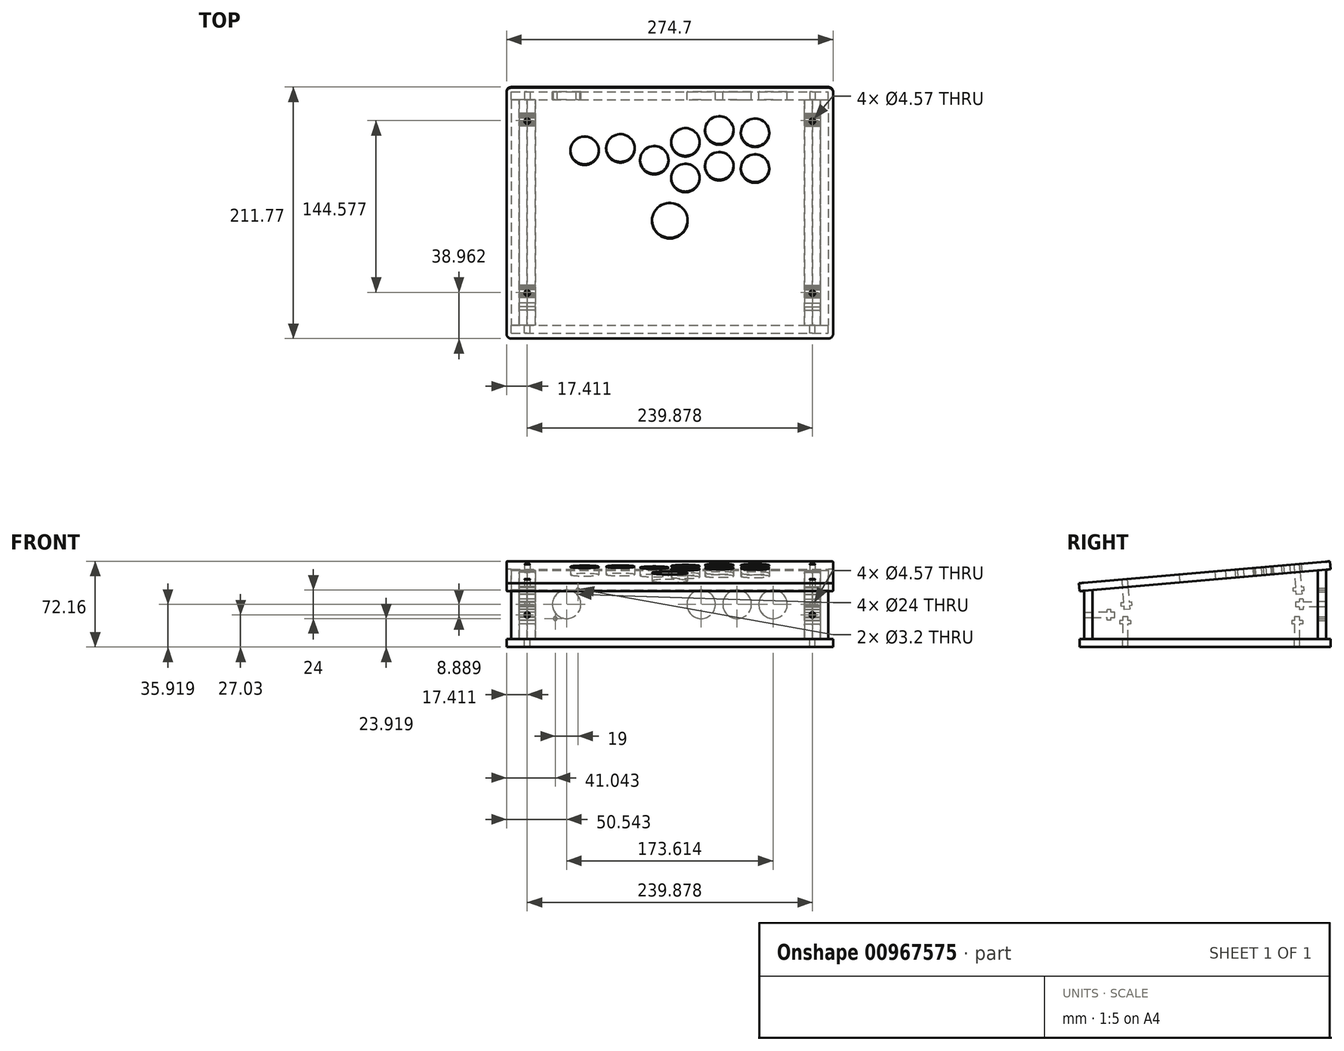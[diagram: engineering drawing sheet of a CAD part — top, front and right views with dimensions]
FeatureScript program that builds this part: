
annotation { "Feature Type Name" : "Feature", "Feature Type Description" : "" }
export const myFeature = defineFeature(function(context is Context, id is Id, definition is map)
    precondition{}
    {
        {
            var Q0;
            Q0=qCreatedBy(makeId("Right.planeOp"),FACE);
            var sketch = newSketch(context, id + "F0", { "sketchPlane" : qUnion([Q0])});
            skLineSegment(sketch, "E0", {"start": v(-101.6, -20.32) * mm, "end": v(101.6, -20.32) * mm});
            skLineSegment(sketch, "E1", {"start": v(101.6, -20.32) * mm, "end": v(101.6, 38.1) * mm});
            skLineSegment(sketch, "E2", {"start": v(101.6, 38.1) * mm, "end": v(-101.6, 20.32) * mm});
            skLineSegment(sketch, "E3", {"start": v(-101.6, 20.32) * mm, "end": v(-101.6, -20.32) * mm});
            skLineSegment(sketch, "E4", {"start": v(94.9, 37.51) * mm, "end": v(94.9, -20.32) * mm});
            skLineSegment(sketch, "E5", {"start": v(-94.9, 20.9) * mm, "end": v(-94.9, -20.32) * mm});
            skLineSegment(sketch, "E6", {"start": v(79.65, -20.32) * mm, "end": v(79.65, -1.63) * mm});
            skLineSegment(sketch, "E7", {"start": v(79.65, -1.63) * mm, "end": v(75.08, -1.63) * mm});
            skLineSegment(sketch, "E8", {"start": v(75.08, -1.63) * mm, "end": v(75.08, -20.32) * mm});
            skLineSegment(sketch, "E9", {"start": v(-64.92, -20.32) * mm, "end": v(-64.92, -1.63) * mm});
            skLineSegment(sketch, "E10", {"start": v(-64.92, -1.63) * mm, "end": v(-69.5, -1.63) * mm});
            skLineSegment(sketch, "E11", {"start": v(-69.5, -1.63) * mm, "end": v(-69.5, -20.32) * mm});
            skLineSegment(sketch, "E12", {"start": v(79.71, 36.18) * mm, "end": v(81.34, 17.56) * mm});
            skLineSegment(sketch, "E13", {"start": v(81.34, 17.56) * mm, "end": v(76.79, 17.16) * mm});
            skLineSegment(sketch, "E14", {"start": v(76.79, 17.16) * mm, "end": v(75.16, 35.78) * mm});
            skLineSegment(sketch, "E15", {"start": v(-65.04, 23.52) * mm, "end": v(-63.4, 4.9) * mm});
            skLineSegment(sketch, "E16", {"start": v(-63.4, 4.9) * mm, "end": v(-67.96, 4.5) * mm});
            skLineSegment(sketch, "E17", {"start": v(-67.96, 4.5) * mm, "end": v(-69.6, 23.12) * mm});
            skLineSegment(sketch, "E18", {"start": v(94.9, 6.6) * mm, "end": v(76.2, 6.6) * mm});
            skLineSegment(sketch, "E19", {"start": v(76.2, 6.6) * mm, "end": v(76.2, 11.17) * mm});
            skLineSegment(sketch, "E20", {"start": v(76.2, 11.17) * mm, "end": v(94.9, 11.17) * mm});
            skLineSegment(sketch, "E21", {"start": v(-94.9, -2.29) * mm, "end": v(-76.2, -2.29) * mm});
            skLineSegment(sketch, "E22", {"start": v(-76.2, -2.29) * mm, "end": v(-76.2, 2.29) * mm});
            skLineSegment(sketch, "E23", {"start": v(-76.2, 2.29) * mm, "end": v(-94.9, 2.29) * mm});
            skPoint(sketch, "E24", {"position": v(-76.2, 0) * mm});
            skPoint(sketch, "E25", {"position": v(76.2, 8.89) * mm});
            skPoint(sketch, "E26", {"position": v(101.6, 8.89) * mm});
            skPoint(sketch, "E27", {"position": v(-101.6, 0) * mm});
            skLineSegment(sketch, "E28.bottom", {"start": v(81.94, -4.67) * mm, "end": v(72.8, -4.67) * mm});
            skLineSegment(sketch, "E28.top", {"start": v(81.94, -7.72) * mm, "end": v(72.8, -7.72) * mm});
            skLineSegment(sketch, "E28.left", {"start": v(81.94, -4.67) * mm, "end": v(81.94, -7.72) * mm});
            skLineSegment(sketch, "E28.right", {"start": v(72.8, -4.67) * mm, "end": v(72.8, -7.72) * mm});
            skLineSegment(sketch, "E29.bottom", {"start": v(-62.64, -4.67) * mm, "end": v(-71.78, -4.67) * mm});
            skLineSegment(sketch, "E29.top", {"start": v(-62.64, -7.72) * mm, "end": v(-71.78, -7.72) * mm});
            skLineSegment(sketch, "E29.left", {"start": v(-62.64, -4.67) * mm, "end": v(-62.64, -7.72) * mm});
            skLineSegment(sketch, "E29.right", {"start": v(-71.78, -4.67) * mm, "end": v(-71.78, -7.72) * mm});
            skLineSegment(sketch, "E30.bottom", {"start": v(-79.25, -4.57) * mm, "end": v(-82.3, -4.57) * mm});
            skLineSegment(sketch, "E30.top", {"start": v(-79.25, 4.57) * mm, "end": v(-82.3, 4.57) * mm});
            skLineSegment(sketch, "E30.left", {"start": v(-79.25, -4.57) * mm, "end": v(-79.25, 4.57) * mm});
            skLineSegment(sketch, "E30.right", {"start": v(-82.3, -4.57) * mm, "end": v(-82.3, 4.57) * mm});
            skLineSegment(sketch, "E31.bottom", {"start": v(-70.5, 7.33) * mm, "end": v(-61.4, 8.13) * mm});
            skLineSegment(sketch, "E31.top", {"start": v(-70.77, 10.37) * mm, "end": v(-61.66, 11.17) * mm});
            skLineSegment(sketch, "E31.left", {"start": v(-70.5, 7.33) * mm, "end": v(-70.77, 10.37) * mm});
            skLineSegment(sketch, "E31.right", {"start": v(-61.4, 8.13) * mm, "end": v(-61.66, 11.17) * mm});
            skLineSegment(sketch, "E32.bottom", {"start": v(74.24, 20) * mm, "end": v(83.35, 20.8) * mm});
            skLineSegment(sketch, "E32.top", {"start": v(73.98, 23.03) * mm, "end": v(83.09, 23.83) * mm});
            skLineSegment(sketch, "E32.left", {"start": v(74.24, 20) * mm, "end": v(73.98, 23.03) * mm});
            skLineSegment(sketch, "E32.right", {"start": v(83.35, 20.8) * mm, "end": v(83.09, 23.83) * mm});
            skLineSegment(sketch, "E33.bottom", {"start": v(82.3, 13.46) * mm, "end": v(79.25, 13.46) * mm});
            skLineSegment(sketch, "E33.top", {"start": v(82.3, 4.32) * mm, "end": v(79.25, 4.32) * mm});
            skLineSegment(sketch, "E33.left", {"start": v(82.3, 13.46) * mm, "end": v(82.3, 4.32) * mm});
            skLineSegment(sketch, "E33.right", {"start": v(79.25, 13.46) * mm, "end": v(79.25, 4.32) * mm});
            skLineSegment(sketch, "E34", {"start": v(79.65, -1.63) * mm, "end": v(81.94, -4.67) * mm, "construction": true});
            skLineSegment(sketch, "E35", {"start": v(75.08, -1.63) * mm, "end": v(72.8, -4.67) * mm, "construction": true});
            skLineSegment(sketch, "E36", {"start": v(79.25, 4.32) * mm, "end": v(76.2, 6.6) * mm, "construction": true});
            skLineSegment(sketch, "E37", {"start": v(76.2, 11.17) * mm, "end": v(79.25, 13.46) * mm, "construction": true});
            skLineSegment(sketch, "E38", {"start": v(81.34, 17.56) * mm, "end": v(83.35, 20.8) * mm, "construction": true});
            skLineSegment(sketch, "E39", {"start": v(76.79, 17.16) * mm, "end": v(74.24, 20) * mm, "construction": true});
            skLineSegment(sketch, "E40", {"start": v(-63.4, 4.9) * mm, "end": v(-61.4, 8.13) * mm, "construction": true});
            skLineSegment(sketch, "E41", {"start": v(-67.96, 4.5) * mm, "end": v(-70.5, 7.33) * mm, "construction": true});
            skLineSegment(sketch, "E42", {"start": v(-76.2, 2.29) * mm, "end": v(-79.25, 4.57) * mm, "construction": true});
            skLineSegment(sketch, "E43", {"start": v(-76.2, -2.29) * mm, "end": v(-79.25, -4.57) * mm, "construction": true});
            skLineSegment(sketch, "E44", {"start": v(-64.92, -1.63) * mm, "end": v(-62.64, -4.67) * mm, "construction": true});
            skLineSegment(sketch, "E45", {"start": v(-69.5, -1.63) * mm, "end": v(-71.78, -4.67) * mm, "construction": true});
            skLineSegment(sketch, "E46", {"start": v(-101.6, 20.32) * mm, "end": v(101.6, 20.32) * mm, "construction": true});
            skSolve(sketch);
        }
        {
            var Q0;
            {var subQ14=sQuery(id+"F0.wireOp",EDGE,"E4");Q0=makeQuery(id+"F0.imprint","IMPRINT",FACE,{"disambiguationData":[TD([[makeQuery(id+"F0.imprint","IMPRINT",EDGE,{"derivedFrom":subQ14}),-1.0]])]});}
            var Q1;
            {var subQ0=sQuery(id+"F0.wireOp",EDGE,"dgdBLiuN-7DTV-gzHf-jHKZ-Ratlxp1D41V1.bottom");Q1=makeQuery(id+"F0.imprint","IMPRINT",FACE,{"disambiguationData":[TD([[makeQuery(id+"F0.imprint","IMPRINT",EDGE,{"derivedFrom":subQ0}),1.0]])]});}
            var Q2;
            {var subQ0=sQuery(id+"F0.wireOp",EDGE,"dgdBLiuN-7DTV-gzHf-jHKZ-Ratlxp1D41V1.top");Q2=makeQuery(id+"F0.imprint","IMPRINT",FACE,{"disambiguationData":[TD([[makeQuery(id+"F0.imprint","IMPRINT",EDGE,{"derivedFrom":subQ0}),-1.0]])]});}
            var Q3;
            {var subQ5=sQuery(id+"F0.wireOp",EDGE,"fHmdqq7Y-QNzh-l0Eo-8w8f-Dmk2epEtvhAU.left");Q3=makeQuery(id+"F0.imprint","IMPRINT",FACE,{"disambiguationData":[TD([[makeQuery(id+"F0.imprint","IMPRINT",EDGE,{"derivedFrom":subQ5}),-1.0]])]});}
            var Q4;
            {var subQ5=sQuery(id+"F0.wireOp",EDGE,"fHmdqq7Y-QNzh-l0Eo-8w8f-Dmk2epEtvhAU.right");Q4=makeQuery(id+"F0.imprint","IMPRINT",FACE,{"disambiguationData":[TD([[makeQuery(id+"F0.imprint","IMPRINT",EDGE,{"derivedFrom":subQ5}),1.0]])]});}
            var Q5;
            {var subQ0=sQuery(id+"F0.wireOp",EDGE,"fHmdqq7Y-QNzh-l0Eo-8w8f-Dmk2epEtvhAU.bottom");var subQ1=sQuery(id+"F0.wireOp",EDGE,"dgdBLiuN-7DTV-gzHf-jHKZ-Ratlxp1D41V1.left");var subQ2=makeQuery(id+"F0.imprint","INTERSECT",VERTEX,{"derivedFrom":[subQ1,subQ0]});Q5=makeQuery(id+"F0.imprint","IMPRINT",FACE,{"disambiguationData":[TD([[makeQuery(id+"F0.imprint","IMPRINT",EDGE,{"disambiguationData":[TD([[subQ2,-1.0]])],"derivedFrom":subQ1}),-1.0]])]});}
            var Q6;
            {var subQ0=sQuery(id+"F0.wireOp",EDGE,"E12");Q6=makeQuery(id+"F0.imprint","IMPRINT",FACE,{"disambiguationData":[TD([[makeQuery(id+"F0.imprint","IMPRINT",EDGE,{"derivedFrom":subQ0}),-1.0]])]});}
            var Q7;
            {var subQ0=sQuery(id+"F0.wireOp",EDGE,"E15");Q7=makeQuery(id+"F0.imprint","IMPRINT",FACE,{"disambiguationData":[TD([[makeQuery(id+"F0.imprint","IMPRINT",EDGE,{"derivedFrom":subQ0}),-1.0]])]});}
            var Q8;
            {var subQ0=sQuery(id+"F0.wireOp",EDGE,"E21");Q8=makeQuery(id+"F0.imprint","IMPRINT",FACE,{"disambiguationData":[TD([[makeQuery(id+"F0.imprint","IMPRINT",EDGE,{"derivedFrom":subQ0}),1.0]])]});}
            var Q9;
            {var subQ0=sQuery(id+"F0.wireOp",EDGE,"E9");Q9=makeQuery(id+"F0.imprint","IMPRINT",FACE,{"disambiguationData":[TD([[makeQuery(id+"F0.imprint","IMPRINT",EDGE,{"derivedFrom":subQ0}),1.0]])]});}
            var Q10;
            {var subQ0=sQuery(id+"F0.wireOp",EDGE,"E6");Q10=makeQuery(id+"F0.imprint","IMPRINT",FACE,{"disambiguationData":[TD([[makeQuery(id+"F0.imprint","IMPRINT",EDGE,{"derivedFrom":subQ0}),1.0]])]});}
            var Q11;
            {var subQ0=sQuery(id+"F0.wireOp",EDGE,"E18");Q11=makeQuery(id+"F0.imprint","IMPRINT",FACE,{"disambiguationData":[TD([[makeQuery(id+"F0.imprint","IMPRINT",EDGE,{"derivedFrom":subQ0}),-1.0]])]});}
            var Q12;
            {var subQ5=sQuery(id+"F0.wireOp",EDGE,"E32.left");Q12=makeQuery(id+"F0.imprint","IMPRINT",FACE,{"disambiguationData":[TD([[makeQuery(id+"F0.imprint","IMPRINT",EDGE,{"derivedFrom":subQ5}),-1.0]])]});}
            var Q13;
            {var subQ5=sQuery(id+"F0.wireOp",EDGE,"E32.right");Q13=makeQuery(id+"F0.imprint","IMPRINT",FACE,{"disambiguationData":[TD([[makeQuery(id+"F0.imprint","IMPRINT",EDGE,{"derivedFrom":subQ5}),1.0]])]});}
            var Q14;
            {var subQ5=sQuery(id+"F0.wireOp",EDGE,"E33.top");Q14=makeQuery(id+"F0.imprint","IMPRINT",FACE,{"disambiguationData":[TD([[makeQuery(id+"F0.imprint","IMPRINT",EDGE,{"derivedFrom":subQ5}),-1.0]])]});}
            var Q15;
            {var subQ5=sQuery(id+"F0.wireOp",EDGE,"E33.bottom");Q15=makeQuery(id+"F0.imprint","IMPRINT",FACE,{"disambiguationData":[TD([[makeQuery(id+"F0.imprint","IMPRINT",EDGE,{"derivedFrom":subQ5}),1.0]])]});}
            var Q16;
            {var subQ5=sQuery(id+"F0.wireOp",EDGE,"E28.left");Q16=makeQuery(id+"F0.imprint","IMPRINT",FACE,{"disambiguationData":[TD([[makeQuery(id+"F0.imprint","IMPRINT",EDGE,{"derivedFrom":subQ5}),-1.0]])]});}
            var Q17;
            {var subQ5=sQuery(id+"F0.wireOp",EDGE,"E28.right");Q17=makeQuery(id+"F0.imprint","IMPRINT",FACE,{"disambiguationData":[TD([[makeQuery(id+"F0.imprint","IMPRINT",EDGE,{"derivedFrom":subQ5}),1.0]])]});}
            var Q18;
            {var subQ5=sQuery(id+"F0.wireOp",EDGE,"E29.left");Q18=makeQuery(id+"F0.imprint","IMPRINT",FACE,{"disambiguationData":[TD([[makeQuery(id+"F0.imprint","IMPRINT",EDGE,{"derivedFrom":subQ5}),-1.0]])]});}
            var Q19;
            {var subQ5=sQuery(id+"F0.wireOp",EDGE,"E29.right");Q19=makeQuery(id+"F0.imprint","IMPRINT",FACE,{"disambiguationData":[TD([[makeQuery(id+"F0.imprint","IMPRINT",EDGE,{"derivedFrom":subQ5}),1.0]])]});}
            var Q20;
            {var subQ5=sQuery(id+"F0.wireOp",EDGE,"E30.bottom");Q20=makeQuery(id+"F0.imprint","IMPRINT",FACE,{"disambiguationData":[TD([[makeQuery(id+"F0.imprint","IMPRINT",EDGE,{"derivedFrom":subQ5}),-1.0]])]});}
            var Q21;
            {var subQ5=sQuery(id+"F0.wireOp",EDGE,"E30.top");Q21=makeQuery(id+"F0.imprint","IMPRINT",FACE,{"disambiguationData":[TD([[makeQuery(id+"F0.imprint","IMPRINT",EDGE,{"derivedFrom":subQ5}),1.0]])]});}
            var Q22;
            {var subQ5=sQuery(id+"F0.wireOp",EDGE,"E31.left");Q22=makeQuery(id+"F0.imprint","IMPRINT",FACE,{"disambiguationData":[TD([[makeQuery(id+"F0.imprint","IMPRINT",EDGE,{"derivedFrom":subQ5}),-1.0]])]});}
            var Q23;
            {var subQ5=sQuery(id+"F0.wireOp",EDGE,"E31.right");Q23=makeQuery(id+"F0.imprint","IMPRINT",FACE,{"disambiguationData":[TD([[makeQuery(id+"F0.imprint","IMPRINT",EDGE,{"derivedFrom":subQ5}),1.0]])]});}
            var Q24;
            {var subQ0=sQuery(id+"F0.wireOp",EDGE,"UAsRLKdk-vdFN-tKB4-pKpE-Und0eIql7xDi");Q24=makeQuery(id+"F0.imprint","IMPRINT",FACE,{"disambiguationData":[TD([[makeQuery(id+"F0.imprint","IMPRINT",EDGE,{"derivedFrom":subQ0}),1.0]])]});}
            extrude(context, id + "F1", {"entities" : qUnion([Q0, Q1, Q2, Q3, Q4, Q5, Q6, Q7, Q8, Q9, Q10, Q11, Q12, Q13, Q14, Q15, Q16, Q17, Q18, Q19, Q20, Q21, Q22, Q23, Q24]), "oppositeDirection" : true, "depth" : 6.7 * mm, "offsetDistance" : 25.4 * mm});
        }
        {
            var Q0;
            {var subQ14=sQuery(id+"F0.wireOp",EDGE,"E4");Q0=makeQuery(id+"F0.imprint","IMPRINT",FACE,{"disambiguationData":[TD([[makeQuery(id+"F0.imprint","IMPRINT",EDGE,{"derivedFrom":subQ14}),-1.0]])]});}
            extrude(context, id + "F2", {"entities" : qUnion([Q0]), "oppositeDirection" : true, "depth" : 6.7 * mm, "offsetDistance" : 25.4 * mm});
        }
        {
            var Q0;
            Q0=makeQuery(id+"F2.opExtrude","SWEPT_BODY",BODY,{"disambiguationData":[OSD([sQuery(id+"F0.wireOp",EDGE,"E0"),sQuery(id+"F0.wireOp",EDGE,"E2"),sQuery(id+"F0.wireOp",EDGE,"E4"),sQuery(id+"F0.wireOp",EDGE,"E5"),sQuery(id+"F0.wireOp",EDGE,"E6"),sQuery(id+"F0.wireOp",EDGE,"E7"),sQuery(id+"F0.wireOp",EDGE,"E8"),sQuery(id+"F0.wireOp",EDGE,"E9"),sQuery(id+"F0.wireOp",EDGE,"E10"),sQuery(id+"F0.wireOp",EDGE,"E11"),sQuery(id+"F0.wireOp",EDGE,"E12"),sQuery(id+"F0.wireOp",EDGE,"E13"),sQuery(id+"F0.wireOp",EDGE,"E14"),sQuery(id+"F0.wireOp",EDGE,"E15"),sQuery(id+"F0.wireOp",EDGE,"E16"),sQuery(id+"F0.wireOp",EDGE,"E17"),sQuery(id+"F0.wireOp",EDGE,"E18"),sQuery(id+"F0.wireOp",EDGE,"E19"),sQuery(id+"F0.wireOp",EDGE,"E20"),sQuery(id+"F0.wireOp",EDGE,"E21"),sQuery(id+"F0.wireOp",EDGE,"E22"),sQuery(id+"F0.wireOp",EDGE,"E23"),sQuery(id+"F0.wireOp",EDGE,"E28.bottom"),sQuery(id+"F0.wireOp",EDGE,"E28.top"),sQuery(id+"F0.wireOp",EDGE,"E28.left"),sQuery(id+"F0.wireOp",EDGE,"E28.right"),sQuery(id+"F0.wireOp",EDGE,"E29.bottom"),sQuery(id+"F0.wireOp",EDGE,"E29.top"),sQuery(id+"F0.wireOp",EDGE,"E29.left"),sQuery(id+"F0.wireOp",EDGE,"E29.right"),sQuery(id+"F0.wireOp",EDGE,"E30.bottom"),sQuery(id+"F0.wireOp",EDGE,"E30.top"),sQuery(id+"F0.wireOp",EDGE,"E30.left"),sQuery(id+"F0.wireOp",EDGE,"E30.right"),sQuery(id+"F0.wireOp",EDGE,"E31.bottom"),sQuery(id+"F0.wireOp",EDGE,"E31.top"),sQuery(id+"F0.wireOp",EDGE,"E31.left"),sQuery(id+"F0.wireOp",EDGE,"E31.right"),sQuery(id+"F0.wireOp",EDGE,"E32.bottom"),sQuery(id+"F0.wireOp",EDGE,"E32.top"),sQuery(id+"F0.wireOp",EDGE,"E32.left"),sQuery(id+"F0.wireOp",EDGE,"E32.right"),sQuery(id+"F0.wireOp",EDGE,"E33.bottom"),sQuery(id+"F0.wireOp",EDGE,"E33.top"),sQuery(id+"F0.wireOp",EDGE,"E33.left"),sQuery(id+"F0.wireOp",EDGE,"E33.right")])]});
            var Q1;
            Q1=makeQuery(id+"F1.opExtrude","SWEPT_EDGE",EDGE,{"disambiguationData":[OSD([sQuery(id+"F0.wireOp",EDGE,"E2"),sQuery(id+"F0.wireOp",EDGE,"E5")])]});
            transform(context, id + "F3", {"entities" : qUnion([Q0]), "transformType" : TransformType.TRANSLATION_ENTITY, "oppositeDirectionEntity" : true, "transformLine" : qUnion([Q1]), "makeCopy" : false});
        }
        {
            var Q0;
            Q0=makeQuery(id+"F2.opExtrude","CAP_FACE",FACE,{"disambiguationData":[OSD([sQuery(id+"F0.wireOp",EDGE,"E0"),sQuery(id+"F0.wireOp",EDGE,"E2"),sQuery(id+"F0.wireOp",EDGE,"E4"),sQuery(id+"F0.wireOp",EDGE,"E5"),sQuery(id+"F0.wireOp",EDGE,"E6"),sQuery(id+"F0.wireOp",EDGE,"E7"),sQuery(id+"F0.wireOp",EDGE,"E8"),sQuery(id+"F0.wireOp",EDGE,"E9"),sQuery(id+"F0.wireOp",EDGE,"E10"),sQuery(id+"F0.wireOp",EDGE,"E11"),sQuery(id+"F0.wireOp",EDGE,"E12"),sQuery(id+"F0.wireOp",EDGE,"E13"),sQuery(id+"F0.wireOp",EDGE,"E14"),sQuery(id+"F0.wireOp",EDGE,"E15"),sQuery(id+"F0.wireOp",EDGE,"E16"),sQuery(id+"F0.wireOp",EDGE,"E17"),sQuery(id+"F0.wireOp",EDGE,"E18"),sQuery(id+"F0.wireOp",EDGE,"E19"),sQuery(id+"F0.wireOp",EDGE,"E20"),sQuery(id+"F0.wireOp",EDGE,"E21"),sQuery(id+"F0.wireOp",EDGE,"E22"),sQuery(id+"F0.wireOp",EDGE,"E23"),sQuery(id+"F0.wireOp",EDGE,"E28.bottom"),sQuery(id+"F0.wireOp",EDGE,"E28.top"),sQuery(id+"F0.wireOp",EDGE,"E28.left"),sQuery(id+"F0.wireOp",EDGE,"E28.right"),sQuery(id+"F0.wireOp",EDGE,"E29.bottom"),sQuery(id+"F0.wireOp",EDGE,"E29.top"),sQuery(id+"F0.wireOp",EDGE,"E29.left"),sQuery(id+"F0.wireOp",EDGE,"E29.right"),sQuery(id+"F0.wireOp",EDGE,"E30.bottom"),sQuery(id+"F0.wireOp",EDGE,"E30.top"),sQuery(id+"F0.wireOp",EDGE,"E30.left"),sQuery(id+"F0.wireOp",EDGE,"E30.right"),sQuery(id+"F0.wireOp",EDGE,"E31.bottom"),sQuery(id+"F0.wireOp",EDGE,"E31.top"),sQuery(id+"F0.wireOp",EDGE,"E31.left"),sQuery(id+"F0.wireOp",EDGE,"E31.right"),sQuery(id+"F0.wireOp",EDGE,"E32.bottom"),sQuery(id+"F0.wireOp",EDGE,"E32.top"),sQuery(id+"F0.wireOp",EDGE,"E32.left"),sQuery(id+"F0.wireOp",EDGE,"E32.right"),sQuery(id+"F0.wireOp",EDGE,"E33.bottom"),sQuery(id+"F0.wireOp",EDGE,"E33.top"),sQuery(id+"F0.wireOp",EDGE,"E33.left"),sQuery(id+"F0.wireOp",EDGE,"E33.right")])],"isStart":false});
            extrude(context, id + "F4", {"entities" : qUnion([Q0]), "depth" : 6.7 * mm, "offsetDistance" : 25.4 * mm});
        }
        {
            var Q0;
            Q0=makeQuery(id+"F1.opExtrude","SWEPT_BODY",BODY,{"disambiguationData":[OSD([sQuery(id+"F0.wireOp",EDGE,"E0"),sQuery(id+"F0.wireOp",EDGE,"E2"),sQuery(id+"F0.wireOp",EDGE,"E4"),sQuery(id+"F0.wireOp",EDGE,"E5"),sQuery(id+"F0.wireOp",EDGE,"dgdBLiuN-7DTV-gzHf-jHKZ-Ratlxp1D41V1.bottom")])]});
            var Q1;
            Q1=makeQuery(id+"F2.opExtrude","SWEPT_BODY",BODY,{"disambiguationData":[OSD([sQuery(id+"F0.wireOp",EDGE,"E0"),sQuery(id+"F0.wireOp",EDGE,"E2"),sQuery(id+"F0.wireOp",EDGE,"E4"),sQuery(id+"F0.wireOp",EDGE,"E5"),sQuery(id+"F0.wireOp",EDGE,"dgdBLiuN-7DTV-gzHf-jHKZ-Ratlxp1D41V1.top"),sQuery(id+"F0.wireOp",EDGE,"dgdBLiuN-7DTV-gzHf-jHKZ-Ratlxp1D41V1.left"),sQuery(id+"F0.wireOp",EDGE,"dgdBLiuN-7DTV-gzHf-jHKZ-Ratlxp1D41V1.right"),sQuery(id+"F0.wireOp",EDGE,"fHmdqq7Y-QNzh-l0Eo-8w8f-Dmk2epEtvhAU.bottom"),sQuery(id+"F0.wireOp",EDGE,"fHmdqq7Y-QNzh-l0Eo-8w8f-Dmk2epEtvhAU.top"),sQuery(id+"F0.wireOp",EDGE,"fHmdqq7Y-QNzh-l0Eo-8w8f-Dmk2epEtvhAU.left"),sQuery(id+"F0.wireOp",EDGE,"fHmdqq7Y-QNzh-l0Eo-8w8f-Dmk2epEtvhAU.right")])]});
            var Q2;
            Q2=makeQuery(id+"F4.opExtrude","SWEPT_BODY",BODY,{"disambiguationData":[OSD([sQuery(id+"F0.wireOp",EDGE,"E0"),sQuery(id+"F0.wireOp",EDGE,"E2"),sQuery(id+"F0.wireOp",EDGE,"E4"),sQuery(id+"F0.wireOp",EDGE,"E5"),sQuery(id+"F0.wireOp",EDGE,"E6"),sQuery(id+"F0.wireOp",EDGE,"E7"),sQuery(id+"F0.wireOp",EDGE,"E8"),sQuery(id+"F0.wireOp",EDGE,"E9"),sQuery(id+"F0.wireOp",EDGE,"E10"),sQuery(id+"F0.wireOp",EDGE,"E11"),sQuery(id+"F0.wireOp",EDGE,"E12"),sQuery(id+"F0.wireOp",EDGE,"E13"),sQuery(id+"F0.wireOp",EDGE,"E14"),sQuery(id+"F0.wireOp",EDGE,"E15"),sQuery(id+"F0.wireOp",EDGE,"E16"),sQuery(id+"F0.wireOp",EDGE,"E17"),sQuery(id+"F0.wireOp",EDGE,"E18"),sQuery(id+"F0.wireOp",EDGE,"E19"),sQuery(id+"F0.wireOp",EDGE,"E20"),sQuery(id+"F0.wireOp",EDGE,"E21"),sQuery(id+"F0.wireOp",EDGE,"E22"),sQuery(id+"F0.wireOp",EDGE,"E23"),sQuery(id+"F0.wireOp",EDGE,"E28.bottom"),sQuery(id+"F0.wireOp",EDGE,"E28.top"),sQuery(id+"F0.wireOp",EDGE,"E28.left"),sQuery(id+"F0.wireOp",EDGE,"E28.right"),sQuery(id+"F0.wireOp",EDGE,"E29.bottom"),sQuery(id+"F0.wireOp",EDGE,"E29.top"),sQuery(id+"F0.wireOp",EDGE,"E29.left"),sQuery(id+"F0.wireOp",EDGE,"E29.right"),sQuery(id+"F0.wireOp",EDGE,"E30.bottom"),sQuery(id+"F0.wireOp",EDGE,"E30.top"),sQuery(id+"F0.wireOp",EDGE,"E30.left"),sQuery(id+"F0.wireOp",EDGE,"E30.right"),sQuery(id+"F0.wireOp",EDGE,"E31.bottom"),sQuery(id+"F0.wireOp",EDGE,"E31.top"),sQuery(id+"F0.wireOp",EDGE,"E31.left"),sQuery(id+"F0.wireOp",EDGE,"E31.right"),sQuery(id+"F0.wireOp",EDGE,"E32.bottom"),sQuery(id+"F0.wireOp",EDGE,"E32.top"),sQuery(id+"F0.wireOp",EDGE,"E32.left"),sQuery(id+"F0.wireOp",EDGE,"E32.right"),sQuery(id+"F0.wireOp",EDGE,"E33.bottom"),sQuery(id+"F0.wireOp",EDGE,"E33.top"),sQuery(id+"F0.wireOp",EDGE,"E33.left"),sQuery(id+"F0.wireOp",EDGE,"E33.right")])]});
            var Q3;
            Q3=qCreatedBy(makeId("Right.planeOp"),FACE);
            mirror(context, id + "F5", {"entities" : qUnion([Q0, Q1, Q2]), "mirrorPlane" : qUnion([Q3])});
        }
        {
            var Q0;
            Q0=makeQuery(id+"F5.opPattern","COPY",BODY,{"derivedFrom":makeQuery(id+"F1.opExtrude","SWEPT_BODY",BODY,{"disambiguationData":[OSD([sQuery(id+"F0.wireOp",EDGE,"E0"),sQuery(id+"F0.wireOp",EDGE,"E2"),sQuery(id+"F0.wireOp",EDGE,"E4"),sQuery(id+"F0.wireOp",EDGE,"E5")])]}),"instanceName":"1"});
            var Q1;
            Q1=makeQuery(id+"F5.opPattern","COPY",BODY,{"derivedFrom":makeQuery(id+"F2.opExtrude","SWEPT_BODY",BODY,{"disambiguationData":[OSD([sQuery(id+"F0.wireOp",EDGE,"E0"),sQuery(id+"F0.wireOp",EDGE,"E2"),sQuery(id+"F0.wireOp",EDGE,"E4"),sQuery(id+"F0.wireOp",EDGE,"E5"),sQuery(id+"F0.wireOp",EDGE,"E6"),sQuery(id+"F0.wireOp",EDGE,"E7"),sQuery(id+"F0.wireOp",EDGE,"E8"),sQuery(id+"F0.wireOp",EDGE,"E9"),sQuery(id+"F0.wireOp",EDGE,"E10"),sQuery(id+"F0.wireOp",EDGE,"E11"),sQuery(id+"F0.wireOp",EDGE,"E12"),sQuery(id+"F0.wireOp",EDGE,"E13"),sQuery(id+"F0.wireOp",EDGE,"E14"),sQuery(id+"F0.wireOp",EDGE,"E15"),sQuery(id+"F0.wireOp",EDGE,"E16"),sQuery(id+"F0.wireOp",EDGE,"E17"),sQuery(id+"F0.wireOp",EDGE,"E18"),sQuery(id+"F0.wireOp",EDGE,"E19"),sQuery(id+"F0.wireOp",EDGE,"E20"),sQuery(id+"F0.wireOp",EDGE,"E21"),sQuery(id+"F0.wireOp",EDGE,"E22"),sQuery(id+"F0.wireOp",EDGE,"E23"),sQuery(id+"F0.wireOp",EDGE,"E28.bottom"),sQuery(id+"F0.wireOp",EDGE,"E28.top"),sQuery(id+"F0.wireOp",EDGE,"E28.left"),sQuery(id+"F0.wireOp",EDGE,"E28.right"),sQuery(id+"F0.wireOp",EDGE,"E29.bottom"),sQuery(id+"F0.wireOp",EDGE,"E29.top"),sQuery(id+"F0.wireOp",EDGE,"E29.left"),sQuery(id+"F0.wireOp",EDGE,"E29.right"),sQuery(id+"F0.wireOp",EDGE,"E30.bottom"),sQuery(id+"F0.wireOp",EDGE,"E30.top"),sQuery(id+"F0.wireOp",EDGE,"E30.left"),sQuery(id+"F0.wireOp",EDGE,"E30.right"),sQuery(id+"F0.wireOp",EDGE,"E31.bottom"),sQuery(id+"F0.wireOp",EDGE,"E31.top"),sQuery(id+"F0.wireOp",EDGE,"E31.left"),sQuery(id+"F0.wireOp",EDGE,"E31.right"),sQuery(id+"F0.wireOp",EDGE,"E32.bottom"),sQuery(id+"F0.wireOp",EDGE,"E32.top"),sQuery(id+"F0.wireOp",EDGE,"E32.left"),sQuery(id+"F0.wireOp",EDGE,"E32.right"),sQuery(id+"F0.wireOp",EDGE,"E33.bottom"),sQuery(id+"F0.wireOp",EDGE,"E33.top"),sQuery(id+"F0.wireOp",EDGE,"E33.left"),sQuery(id+"F0.wireOp",EDGE,"E33.right")])]}),"instanceName":"1"});
            var Q2;
            Q2=makeQuery(id+"F5.opPattern","COPY",BODY,{"derivedFrom":makeQuery(id+"F4.opExtrude","SWEPT_BODY",BODY,{"disambiguationData":[OSD([sQuery(id+"F0.wireOp",EDGE,"E0"),sQuery(id+"F0.wireOp",EDGE,"E2"),sQuery(id+"F0.wireOp",EDGE,"E4"),sQuery(id+"F0.wireOp",EDGE,"E5"),sQuery(id+"F0.wireOp",EDGE,"E6"),sQuery(id+"F0.wireOp",EDGE,"E7"),sQuery(id+"F0.wireOp",EDGE,"E8"),sQuery(id+"F0.wireOp",EDGE,"E9"),sQuery(id+"F0.wireOp",EDGE,"E10"),sQuery(id+"F0.wireOp",EDGE,"E11"),sQuery(id+"F0.wireOp",EDGE,"E12"),sQuery(id+"F0.wireOp",EDGE,"E13"),sQuery(id+"F0.wireOp",EDGE,"E14"),sQuery(id+"F0.wireOp",EDGE,"E15"),sQuery(id+"F0.wireOp",EDGE,"E16"),sQuery(id+"F0.wireOp",EDGE,"E17"),sQuery(id+"F0.wireOp",EDGE,"E18"),sQuery(id+"F0.wireOp",EDGE,"E19"),sQuery(id+"F0.wireOp",EDGE,"E20"),sQuery(id+"F0.wireOp",EDGE,"E21"),sQuery(id+"F0.wireOp",EDGE,"E22"),sQuery(id+"F0.wireOp",EDGE,"E23"),sQuery(id+"F0.wireOp",EDGE,"E28.bottom"),sQuery(id+"F0.wireOp",EDGE,"E28.top"),sQuery(id+"F0.wireOp",EDGE,"E28.left"),sQuery(id+"F0.wireOp",EDGE,"E28.right"),sQuery(id+"F0.wireOp",EDGE,"E29.bottom"),sQuery(id+"F0.wireOp",EDGE,"E29.top"),sQuery(id+"F0.wireOp",EDGE,"E29.left"),sQuery(id+"F0.wireOp",EDGE,"E29.right"),sQuery(id+"F0.wireOp",EDGE,"E30.bottom"),sQuery(id+"F0.wireOp",EDGE,"E30.top"),sQuery(id+"F0.wireOp",EDGE,"E30.left"),sQuery(id+"F0.wireOp",EDGE,"E30.right"),sQuery(id+"F0.wireOp",EDGE,"E31.bottom"),sQuery(id+"F0.wireOp",EDGE,"E31.top"),sQuery(id+"F0.wireOp",EDGE,"E31.left"),sQuery(id+"F0.wireOp",EDGE,"E31.right"),sQuery(id+"F0.wireOp",EDGE,"E32.bottom"),sQuery(id+"F0.wireOp",EDGE,"E32.top"),sQuery(id+"F0.wireOp",EDGE,"E32.left"),sQuery(id+"F0.wireOp",EDGE,"E32.right"),sQuery(id+"F0.wireOp",EDGE,"E33.bottom"),sQuery(id+"F0.wireOp",EDGE,"E33.top"),sQuery(id+"F0.wireOp",EDGE,"E33.left"),sQuery(id+"F0.wireOp",EDGE,"E33.right")])]}),"instanceName":"1"});
            transform(context, id + "F6", {"entities" : qUnion([Q0, Q1, Q2]), "transformType" : TransformType.TRANSLATION_3D, "dx" : -266.7 * mm, "dy" : 0 * mm, "dz" : 0 * mm, "makeCopy" : false});
        }
        {
            var Q0;
            {var subQ0=sQuery(id+"F0.wireOp",EDGE,"E3");Q0=makeQuery(id+"F0.imprint","IMPRINT",FACE,{"disambiguationData":[TD([[makeQuery(id+"F0.imprint","IMPRINT",EDGE,{"derivedFrom":subQ0}),1.0]])]});}
            var Q1;
            {var subQ0=sQuery(id+"F0.wireOp",EDGE,"E1");Q1=makeQuery(id+"F0.imprint","IMPRINT",FACE,{"disambiguationData":[TD([[makeQuery(id+"F0.imprint","IMPRINT",EDGE,{"derivedFrom":subQ0}),1.0]])]});}
            var Q2;
            Q2=makeQuery(id+"F5.opPattern","COPY",FACE,{"derivedFrom":makeQuery(id+"F1.opExtrude","CAP_FACE",FACE,{"disambiguationData":[OSD([sQuery(id+"F0.wireOp",EDGE,"E0"),sQuery(id+"F0.wireOp",EDGE,"E2"),sQuery(id+"F0.wireOp",EDGE,"E4"),sQuery(id+"F0.wireOp",EDGE,"E5")])],"isStart":true}),"instanceName":"1"});
            extrude(context, id + "F7", {"entities" : qUnion([Q0, Q1]), "endBound" : BoundingType.UP_TO_SURFACE, "oppositeDirection" : true, "depth" : 254 * mm, "endBoundEntityFace" : qUnion([Q2]), "offsetDistance" : 25.4 * mm});
        }
        {
            var Q0;
            Q0=makeQuery(id+"F7.opExtrude","SWEPT_FACE",FACE,{"disambiguationData":[OSD([sQuery(id+"F0.wireOp",EDGE,"E5")])]});
            var sketch = newSketch(context, id + "F8", { "sketchPlane" : qUnion([Q0])});
            skCircle(sketch, "E47", {"center": v(253.29, 0) * mm, "radius": 2.29 * mm});
            skCircle(sketch, "E48", {"center": v(13.41, 0) * mm, "radius": 2.29 * mm});
            skSolve(sketch);
        }
        {
            var Q0;
            Q0=makeQuery(id+"F7.opExtrude","SWEPT_FACE",FACE,{"disambiguationData":[OSD([sQuery(id+"F0.wireOp",EDGE,"E4")])]});
            var sketch = newSketch(context, id + "F9", { "sketchPlane" : qUnion([Q0])});
            skCircle(sketch, "E49", {"center": v(-253.29, 8.89) * mm, "radius": 2.29 * mm});
            skCircle(sketch, "E50", {"center": v(-13.41, 8.89) * mm, "radius": 2.29 * mm});
            skSolve(sketch);
        }
        {
            var Q0;
            Q0 = qSketchRegion(id + "F8", true);
            extrude(context, id + "F10", {"entities" : qUnion([Q0]), "operationType" : NewBodyOperationType.REMOVE, "endBound" : BoundingType.UP_TO_NEXT, "oppositeDirection" : true, "depth" : 25.4 * mm, "offsetDistance" : 25.4 * mm});
        }
        {
            var Q0;
            Q0 = qSketchRegion(id + "F9", true);
            extrude(context, id + "F11", {"entities" : qUnion([Q0]), "operationType" : NewBodyOperationType.REMOVE, "endBound" : BoundingType.UP_TO_NEXT, "oppositeDirection" : true, "depth" : 25.4 * mm, "offsetDistance" : 25.4 * mm});
        }
        {
            var Q0;
            Q0=makeQuery(id+"F1.opExtrude","SWEPT_FACE",FACE,{"disambiguationData":[OSD([sQuery(id+"F0.wireOp",EDGE,"E2")])]});
            var sketch = newSketch(context, id + "F12", { "sketchPlane" : qUnion([Q0])});
            skCircle(sketch, "E51", {"center": v(-133.35, -3.85) * mm, "radius": 15 * mm});
            skCircle(sketch, "E52", {"center": v(-205.06, 55.3) * mm, "radius": 12 * mm});
            skCircle(sketch, "E53", {"center": v(-174.92, 57.3) * mm, "radius": 12 * mm});
            skCircle(sketch, "E54", {"center": v(-146.43, 47.3) * mm, "radius": 12 * mm});
            skCircle(sketch, "E55", {"center": v(-120.27, 62.4) * mm, "radius": 12 * mm});
            skCircle(sketch, "E56", {"center": v(-91.78, 72.4) * mm, "radius": 12 * mm});
            skCircle(sketch, "E57", {"center": v(-61.64, 70.4) * mm, "radius": 12 * mm});
            skCircle(sketch, "E58", {"center": v(-120.27, 32.2) * mm, "radius": 12 * mm});
            skCircle(sketch, "E59", {"center": v(-91.78, 42.2) * mm, "radius": 12 * mm});
            skCircle(sketch, "E60", {"center": v(-61.64, 40.2) * mm, "radius": 12 * mm});
            skCircle(sketch, "E61", {"center": v(-205.06, 55.3) * mm, "radius": 13.6 * mm, "construction": true});
            skCircle(sketch, "E62", {"center": v(-174.92, 57.3) * mm, "radius": 13.6 * mm, "construction": true});
            skCircle(sketch, "E63", {"center": v(-146.43, 47.3) * mm, "radius": 13.6 * mm, "construction": true});
            skCircle(sketch, "E64", {"center": v(-120.27, 62.4) * mm, "radius": 13.6 * mm, "construction": true});
            skCircle(sketch, "E65", {"center": v(-91.78, 72.4) * mm, "radius": 13.6 * mm, "construction": true});
            skCircle(sketch, "E66", {"center": v(-61.64, 70.4) * mm, "radius": 13.6 * mm, "construction": true});
            skCircle(sketch, "E67", {"center": v(-120.27, 32.2) * mm, "radius": 13.6 * mm, "construction": true});
            skCircle(sketch, "E68", {"center": v(-91.78, 42.2) * mm, "radius": 13.6 * mm, "construction": true});
            skCircle(sketch, "E69", {"center": v(-61.64, 40.2) * mm, "radius": 13.6 * mm, "construction": true});
            skCircle(sketch, "E70", {"center": v(-133.35, -3.85) * mm, "radius": 16.75 * mm, "construction": true});
            skLineSegment(sketch, "E71", {"start": v(-120.27, 32.2) * mm, "end": v(-91.78, 42.2) * mm, "construction": true});
            skLineSegment(sketch, "E72", {"start": v(-91.78, 42.2) * mm, "end": v(-61.64, 40.2) * mm, "construction": true});
            skLineSegment(sketch, "E73", {"start": v(-91.78, 42.2) * mm, "end": v(-91.78, 72.4) * mm, "construction": true});
            skLineSegment(sketch, "E74", {"start": v(-61.64, 40.2) * mm, "end": v(-61.64, 70.4) * mm, "construction": true});
            skLineSegment(sketch, "E75", {"start": v(-205.06, 55.3) * mm, "end": v(-174.92, 57.3) * mm, "construction": true});
            skLineSegment(sketch, "E76", {"start": v(-174.92, 57.3) * mm, "end": v(-146.43, 47.3) * mm, "construction": true});
            skLineSegment(sketch, "E77", {"start": v(-146.43, 47.3) * mm, "end": v(-120.27, 32.2) * mm, "construction": true});
            skLineSegment(sketch, "E78", {"start": v(-146.43, 47.3) * mm, "end": v(-120.27, 62.4) * mm, "construction": true});
            skLineSegment(sketch, "E79", {"start": v(-120.27, 62.4) * mm, "end": v(-91.78, 72.4) * mm, "construction": true});
            skLineSegment(sketch, "E80", {"start": v(-91.78, 72.4) * mm, "end": v(-61.64, 70.4) * mm, "construction": true});
            skLineSegment(sketch, "E81", {"start": v(-120.27, 32.2) * mm, "end": v(-120.27, 62.4) * mm, "construction": true});
            skLineSegment(sketch, "E82", {"start": v(-146.43, 47.3) * mm, "end": v(-120.27, 47.3) * mm, "construction": true});
            skPoint(sketch, "E83", {"position": v(-133.35, 47.3) * mm});
            skCircle(sketch, "E84", {"center": v(-253.29, -65.03) * mm, "radius": 2.29 * mm});
            skCircle(sketch, "E85", {"center": v(-13.41, -65.03) * mm, "radius": 2.29 * mm});
            skCircle(sketch, "E86", {"center": v(-13.41, 80.28) * mm, "radius": 2.29 * mm});
            skCircle(sketch, "E87", {"center": v(-253.29, 80.28) * mm, "radius": 2.29 * mm});
            skLineSegment(sketch, "E88", {"start": v(-133.35, 104.53) * mm, "end": v(-133.35, -99.44) * mm, "construction": true});
            skLineSegment(sketch, "E89.bottom", {"start": v(-266.7, 104.53) * mm, "end": v(0, 104.53) * mm});
            skLineSegment(sketch, "E89.top", {"start": v(-266.7, -99.44) * mm, "end": v(0, -99.44) * mm});
            skLineSegment(sketch, "E89.left", {"start": v(-266.7, 104.53) * mm, "end": v(-266.7, -99.44) * mm});
            skLineSegment(sketch, "E89.right", {"start": v(0, 104.53) * mm, "end": v(0, -99.44) * mm});
            skLineSegment(sketch, "E90.0", {"start": v(-270.7, 104.53) * mm, "end": v(-270.7, -99.44) * mm});
            skLineSegment(sketch, "E90.1", {"start": v(-266.7, 108.53) * mm, "end": v(0, 108.53) * mm});
            skLineSegment(sketch, "E90.2", {"start": v(4, 104.53) * mm, "end": v(4, -99.44) * mm});
            skLineSegment(sketch, "E90.3", {"start": v(-266.7, -103.44) * mm, "end": v(0, -103.44) * mm});
            skPoint(sketch, "E91.visualSharp", {"position": v(-270.7, 108.53) * mm});
            skArc(sketch, "E91.filletArc", {"start": v(-266.7, 108.53) * mm, "mid": v(-269.53, 107.36) * mm, "end": v(-270.7, 104.53) * mm});
            skPoint(sketch, "E92.visualSharp", {"position": v(4, 108.53) * mm});
            skArc(sketch, "E92.filletArc", {"start": v(4, 104.53) * mm, "mid": v(2.83, 107.36) * mm, "end": v(0, 108.53) * mm});
            skPoint(sketch, "E93.visualSharp", {"position": v(4, -103.44) * mm});
            skArc(sketch, "E93.filletArc", {"start": v(0, -103.44) * mm, "mid": v(2.83, -102.27) * mm, "end": v(4, -99.44) * mm});
            skPoint(sketch, "E94.visualSharp", {"position": v(-270.7, -103.44) * mm});
            skArc(sketch, "E94.filletArc", {"start": v(-270.7, -99.44) * mm, "mid": v(-269.53, -102.27) * mm, "end": v(-266.7, -103.44) * mm});
            skLineSegment(sketch, "E95", {"start": v(-133.35, -3.85) * mm, "end": v(-120.27, 32.2) * mm, "construction": true});
            skSolve(sketch);
        }
        {
            var Q0;
            Q0 = qSketchRegion(id + "F12", true);
            var Q1;
            Q1=makeQuery(id+"F12.imprint","IMPRINT",FACE,{"disambiguationData":[TD([[makeQuery(id+"F12.imprint","IMPRINT",EDGE,{"derivedFrom":sQuery(id+"F12.wireOp",EDGE,"E51")}),-1.0]])]});
            var Q2;
            {var subQ1=sQuery(id+"F0.wireOp",EDGE,"E2");Q2=makeQuery(id+"F12.imprint","IMPRINT",FACE,{"disambiguationData":[TD([[makeQuery(id+"F12.imprint","IMPRINT",EDGE,{"derivedFrom":makeQuery(id+"F1.opExtrude","CAP_EDGE",EDGE,{"disambiguationData":[OSD([subQ1])],"isStart":false})}),1.0]])]});}
            extrude(context, id + "F13", {"entities" : qUnion([Q0, Q1, Q2]), "depth" : 6.7 * mm, "offsetDistance" : 25.4 * mm});
        }
        {
            var Q0;
            Q0=makeQuery(id+"F1.opExtrude","SWEPT_FACE",FACE,{"disambiguationData":[OSD([sQuery(id+"F0.wireOp",EDGE,"E0")])]});
            var sketch = newSketch(context, id + "F14", { "sketchPlane" : qUnion([Q0])});
            skLineSegment(sketch, "E96.bottom", {"start": v(0, 101.6) * mm, "end": v(-266.7, 101.6) * mm});
            skLineSegment(sketch, "E96.top", {"start": v(0, -101.6) * mm, "end": v(-266.7, -101.6) * mm});
            skLineSegment(sketch, "E96.left", {"start": v(-266.7, 101.6) * mm, "end": v(-266.7, -101.6) * mm});
            skLineSegment(sketch, "E96.right", {"start": v(0, 101.6) * mm, "end": v(0, -101.6) * mm});
            skCircle(sketch, "E97", {"center": v(-253.29, 67.2) * mm, "radius": 2.29 * mm});
            skCircle(sketch, "E98", {"center": v(-253.29, -77.37) * mm, "radius": 2.29 * mm});
            skCircle(sketch, "E99", {"center": v(-13.41, -77.37) * mm, "radius": 2.29 * mm});
            skCircle(sketch, "E100", {"center": v(-13.41, 67.2) * mm, "radius": 2.29 * mm});
            skLineSegment(sketch, "E101.0", {"start": v(-270.7, 101.6) * mm, "end": v(-270.7, -101.6) * mm});
            skLineSegment(sketch, "E101.1", {"start": v(0, 105.6) * mm, "end": v(-266.7, 105.6) * mm});
            skLineSegment(sketch, "E101.2", {"start": v(4, 101.6) * mm, "end": v(4, -101.6) * mm});
            skLineSegment(sketch, "E101.3", {"start": v(0, -105.6) * mm, "end": v(-266.7, -105.6) * mm});
            skPoint(sketch, "E102.visualSharp", {"position": v(-270.7, 105.6) * mm});
            skArc(sketch, "E102.filletArc", {"start": v(-266.7, 105.6) * mm, "mid": v(-269.53, 104.43) * mm, "end": v(-270.7, 101.6) * mm});
            skPoint(sketch, "E103.visualSharp", {"position": v(4, 105.6) * mm});
            skArc(sketch, "E103.filletArc", {"start": v(4, 101.6) * mm, "mid": v(2.83, 104.43) * mm, "end": v(0, 105.6) * mm});
            skPoint(sketch, "E104.visualSharp", {"position": v(4, -105.6) * mm});
            skArc(sketch, "E104.filletArc", {"start": v(0, -105.6) * mm, "mid": v(2.83, -104.43) * mm, "end": v(4, -101.6) * mm});
            skPoint(sketch, "E105.visualSharp", {"position": v(-270.7, -105.6) * mm});
            skArc(sketch, "E105.filletArc", {"start": v(-270.7, -101.6) * mm, "mid": v(-269.53, -104.43) * mm, "end": v(-266.7, -105.6) * mm});
            skSolve(sketch);
        }
        {
            var Q0;
            Q0 = qSketchRegion(id + "F14", true);
            var Q1;
            {var subQ4=sQuery(id+"F14.wireOp",EDGE,"E96.bottom");Q1=makeQuery(id+"F14.imprint","IMPRINT",FACE,{"disambiguationData":[TD([[makeQuery(id+"F14.imprint","IMPRINT",EDGE,{"derivedFrom":subQ4}),1.0]])]});}
            var Q2;
            {var subQ1=sQuery(id+"F0.wireOp",EDGE,"E0");Q2=makeQuery(id+"F14.imprint","IMPRINT",FACE,{"disambiguationData":[TD([[makeQuery(id+"F14.imprint","IMPRINT",EDGE,{"derivedFrom":makeQuery(id+"F1.opExtrude","CAP_EDGE",EDGE,{"disambiguationData":[OSD([subQ1])],"isStart":false})}),1.0]])]});}
            extrude(context, id + "F15", {"entities" : qUnion([Q0, Q1, Q2]), "depth" : 6.7 * mm, "offsetDistance" : 25.4 * mm});
        }
        {
            var Q0;
            Q0=makeQuery(id+"F7.opExtrude","SWEPT_FACE",FACE,{"disambiguationData":[OSD([sQuery(id+"F0.wireOp",EDGE,"E1")])]});
            var sketch = newSketch(context, id + "F16", { "sketchPlane" : qUnion([Q0])});
            skCircle(sketch, "E106", {"center": v(46.54, 8.89) * mm, "radius": 12 * mm});
            skCircle(sketch, "E107", {"center": v(76.74, 8.89) * mm, "radius": 12 * mm});
            skCircle(sketch, "E108", {"center": v(220.16, 8.89) * mm, "radius": 12 * mm});
            skCircle(sketch, "E109", {"center": v(106.94, 8.89) * mm, "radius": 12 * mm});
            skCircle(sketch, "E110", {"center": v(46.54, 8.89) * mm, "radius": 13.6 * mm, "construction": true});
            skCircle(sketch, "E111", {"center": v(76.74, 8.89) * mm, "radius": 13.6 * mm, "construction": true});
            skCircle(sketch, "E112", {"center": v(106.94, 8.89) * mm, "radius": 13.6 * mm, "construction": true});
            skLineSegment(sketch, "E113.bottom", {"start": v(229.66, -3.11) * mm, "end": v(210.66, -3.11) * mm, "construction": true});
            skLineSegment(sketch, "E113.top", {"start": v(229.66, 20.89) * mm, "end": v(210.66, 20.89) * mm, "construction": true});
            skLineSegment(sketch, "E113.left", {"start": v(229.66, -3.11) * mm, "end": v(229.66, 20.89) * mm, "construction": true});
            skLineSegment(sketch, "E113.right", {"start": v(210.66, -3.11) * mm, "end": v(210.66, 20.89) * mm, "construction": true});
            skCircle(sketch, "E114", {"center": v(210.66, 20.89) * mm, "radius": 1.6 * mm});
            skCircle(sketch, "E115", {"center": v(229.66, -3.11) * mm, "radius": 1.6 * mm});
            skPoint(sketch, "E116", {"position": v(253.29, 8.89) * mm});
            skPoint(sketch, "E117", {"position": v(13.41, 8.89) * mm});
            skLineSegment(sketch, "E118", {"start": v(46.54, 8.89) * mm, "end": v(76.74, 8.89) * mm, "construction": true});
            skLineSegment(sketch, "E119", {"start": v(76.74, 8.89) * mm, "end": v(106.94, 8.89) * mm, "construction": true});
            skPoint(sketch, "E120", {"position": v(61.64, 41.8) * mm});
            skPoint(sketch, "E121", {"position": v(91.78, 41.98) * mm});
            skPoint(sketch, "E122", {"position": v(174.92, 40.66) * mm});
            skPoint(sketch, "E123", {"position": v(205.06, 40.49) * mm});
            skPoint(sketch, "E124", {"position": v(61.64, 8.89) * mm});
            skLineSegment(sketch, "E125", {"start": v(46.54, 8.89) * mm, "end": v(13.41, 8.89) * mm, "construction": true});
            skLineSegment(sketch, "E126", {"start": v(220.16, 8.89) * mm, "end": v(253.29, 8.89) * mm, "construction": true});
            skSolve(sketch);
        }
        {
            var Q0;
            Q0=makeQuery(id+"F16.imprint","IMPRINT",FACE,{"disambiguationData":[TD([[makeQuery(id+"F16.imprint","IMPRINT",EDGE,{"derivedFrom":sQuery(id+"F16.wireOp",EDGE,"E106")}),1.0]])]});
            var Q1;
            Q1=makeQuery(id+"F16.imprint","IMPRINT",FACE,{"disambiguationData":[TD([[makeQuery(id+"F16.imprint","IMPRINT",EDGE,{"derivedFrom":sQuery(id+"F16.wireOp",EDGE,"E107")}),1.0]])]});
            var Q2;
            Q2=makeQuery(id+"F16.imprint","IMPRINT",FACE,{"disambiguationData":[TD([[makeQuery(id+"F16.imprint","IMPRINT",EDGE,{"derivedFrom":sQuery(id+"F16.wireOp",EDGE,"E108")}),1.0]])]});
            var Q3;
            Q3=makeQuery(id+"F16.imprint","IMPRINT",FACE,{"disambiguationData":[TD([[makeQuery(id+"F16.imprint","IMPRINT",EDGE,{"derivedFrom":sQuery(id+"F16.wireOp",EDGE,"E109")}),1.0]])]});
            var Q4;
            Q4=makeQuery(id+"F16.imprint","IMPRINT",FACE,{"disambiguationData":[TD([[makeQuery(id+"F16.imprint","IMPRINT",EDGE,{"derivedFrom":sQuery(id+"F16.wireOp",EDGE,"B3YBxAYl-TvdG-dkWF-egrn-aJtRSMjf0zk2")}),1.0]])]});
            var Q5;
            Q5=makeQuery(id+"F16.imprint","IMPRINT",FACE,{"disambiguationData":[TD([[makeQuery(id+"F16.imprint","IMPRINT",EDGE,{"derivedFrom":sQuery(id+"F16.wireOp",EDGE,"E114")}),1.0]])]});
            var Q6;
            Q6=makeQuery(id+"F16.imprint","IMPRINT",FACE,{"disambiguationData":[TD([[makeQuery(id+"F16.imprint","IMPRINT",EDGE,{"derivedFrom":sQuery(id+"F16.wireOp",EDGE,"E115")}),1.0]])]});
            extrude(context, id + "F17", {"entities" : qUnion([Q0, Q1, Q2, Q3, Q4, Q5, Q6]), "operationType" : NewBodyOperationType.REMOVE, "endBound" : BoundingType.UP_TO_NEXT, "oppositeDirection" : true, "depth" : 25.4 * mm, "offsetDistance" : 25.4 * mm});
        }
    });
